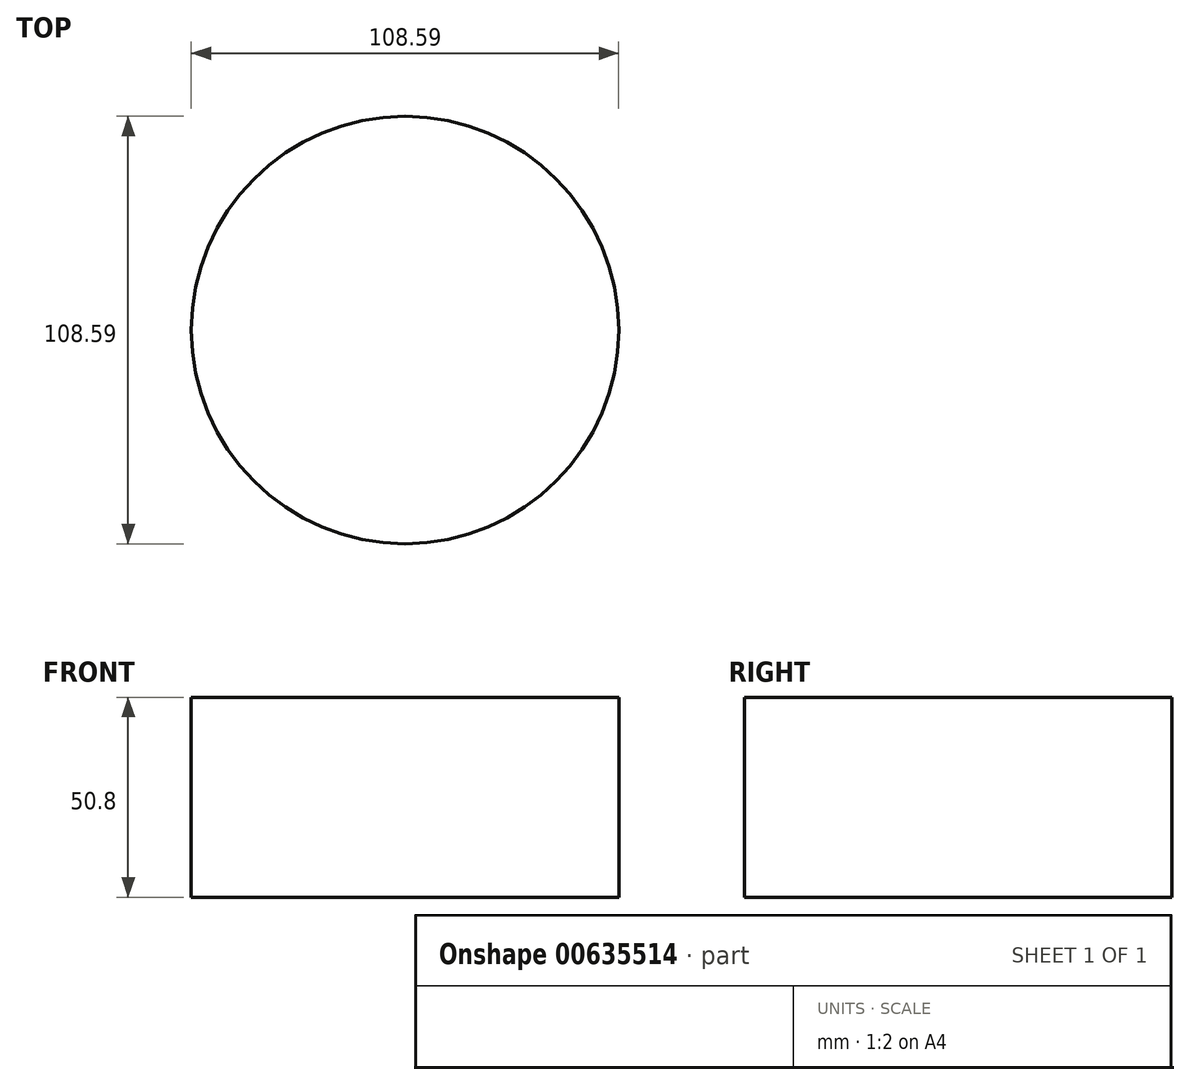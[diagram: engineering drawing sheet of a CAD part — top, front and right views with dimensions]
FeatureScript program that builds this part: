
annotation { "Feature Type Name" : "Feature", "Feature Type Description" : "" }
export const myFeature = defineFeature(function(context is Context, id is Id, definition is map)
    precondition{}
    {
        {
            var Q0;
            Q0=qCreatedBy(makeId("Top.planeOp"),FACE);
            var sketch = newSketch(context, id + "F0", { "sketchPlane" : qUnion([Q0])});
            skCircle(sketch, "E0", {"center": v(-2.2, -2.43) * mm, "radius": 54.3 * mm});
            skPoint(sketch, "E0.first.point", {"position": v(-55.66, -11.92) * mm});
            skPoint(sketch, "E0.second.point", {"position": v(52.04, 0) * mm});
            skPoint(sketch, "E0.third.point", {"position": v(-8.18, 51.54) * mm});
            skSolve(sketch);
        }
        {
            var Q0;
            Q0=makeQuery(id+"F0.imprint","IMPRINT",FACE,{"disambiguationData":[TD([[makeQuery(id+"F0.imprint","IMPRINT",EDGE,{"derivedFrom":sQuery(id+"F0.wireOp",EDGE,"E0")}),1.0]])]});
            extrude(context, id + "F1", {"entities" : qUnion([Q0]), "depth" : 50.8 * mm, "offsetDistance" : 25.4 * mm});
        }
    });
